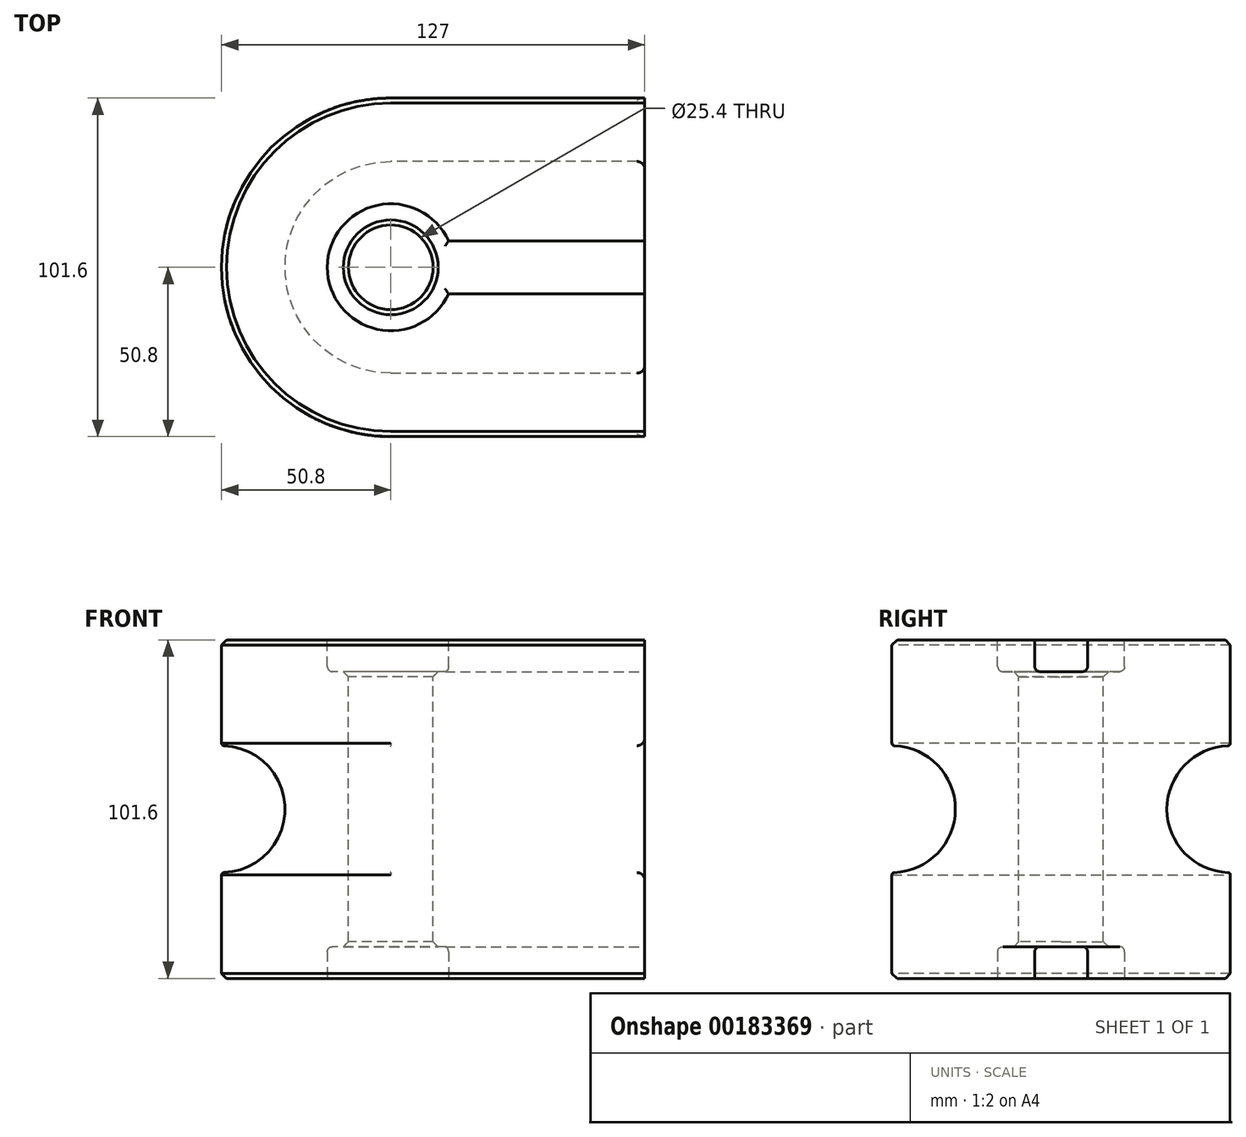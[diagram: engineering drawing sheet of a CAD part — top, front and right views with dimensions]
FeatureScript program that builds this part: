
annotation { "Feature Type Name" : "Feature", "Feature Type Description" : "" }
export const myFeature = defineFeature(function(context is Context, id is Id, definition is map)
    precondition{}
    {
        {
            var Q0;
            Q0=qCreatedBy(makeId("Top.planeOp"),FACE);
            var sketch = newSketch(context, id + "F0", { "sketchPlane" : qUnion([Q0])});
            skArc(sketch, "E0", {"start": v(0, 50.8) * mm, "mid": v(-50.8, 0) * mm, "end": v(0, -50.8) * mm});
            skLineSegment(sketch, "E1", {"start": v(0, -58.97) * mm, "end": v(0, 68.43) * mm, "construction": true});
            skLineSegment(sketch, "E2", {"start": v(0, 50.8) * mm, "end": v(76.2, 50.8) * mm});
            skLineSegment(sketch, "E3", {"start": v(76.2, 50.8) * mm, "end": v(76.2, -50.8) * mm});
            skLineSegment(sketch, "E4", {"start": v(0, -50.8) * mm, "end": v(76.2, -50.8) * mm});
            skSolve(sketch);
        }
        {
            var Q0;
            Q0 = qSketchRegion(id + "F0", true);
            extrude(context, id + "F1", {"entities" : qUnion([Q0]), "endBound" : BoundingType.SYMMETRIC, "depth" : 101.6 * mm});
        }
        {
            var Q0;
            Q0=qCreatedBy(makeId("Top.planeOp"),FACE);
            var sketch = newSketch(context, id + "F2", { "sketchPlane" : qUnion([Q0])});
            skLineSegment(sketch, "E5.0", {"start": v(-0.01, 50.8) * mm, "end": v(88.89, 50.8) * mm});
            skArc(sketch, "E6.0", {"start": v(-0.01, 50.8) * mm, "mid": v(-50.81, 0) * mm, "end": v(-0.01, -50.8) * mm});
            skLineSegment(sketch, "E7.0", {"start": v(-0.01, -50.8) * mm, "end": v(88.89, -50.8) * mm});
            skSolve(sketch);
        }
        {
            var Q0;
            Q0=sQuery(id+"F2.wireOp",VERTEX,"E5.0.end");
            var Q1;
            Q1=sQuery(id+"F2.wireOp",EDGE,"E5.0");
            cPlane(context, id + "F3", {"entities" : qUnion([Q0, Q1]), "cplaneType" : CPlaneType.LINE_POINT, "offset" : 25.4 * mm, "width" : 152.4 * mm, "height" : 152.4 * mm});
        }
        {
            var Q0;
            Q0=qCreatedBy(id+"F3.planeOp",FACE);
            var sketch = newSketch(context, id + "F4", { "sketchPlane" : qUnion([Q0])});
            skCircle(sketch, "E8", {"center": v(50.8, 0) * mm, "radius": 19.05 * mm});
            skSolve(sketch);
        }
        {
            var Q0;
            Q0=makeQuery(id+"F4.imprint","IMPRINT",FACE,{"disambiguationData":[TD([[makeQuery(id+"F4.imprint","IMPRINT",EDGE,{"derivedFrom":sQuery(id+"F4.wireOp",EDGE,"E8")}),1.0]])]});
            var Q1;
            Q1 = qConstructionFilter(qBodyType(qCreatedBy(id + "F2" ,EDGE), BodyType.WIRE), ConstructionObject.NO);
            sweep(context, id + "F5", {"operationType" : NewBodyOperationType.REMOVE, "profiles" : qUnion([Q0]), "path" : qUnion([Q1])});
        }
        {
            var Q0;
            Q0=makeQuery(id+"F1.opExtrude","CAP_FACE",FACE,{"disambiguationData":[OSD([sQuery(id+"F0.wireOp",EDGE,"E0"),sQuery(id+"F0.wireOp",EDGE,"E2"),sQuery(id+"F0.wireOp",EDGE,"E3"),sQuery(id+"F0.wireOp",EDGE,"E4")])],"isStart":false});
            var sketch = newSketch(context, id + "F6", { "sketchPlane" : qUnion([Q0])});
            skCircle(sketch, "E9", {"center": v(0, 0) * mm, "radius": 12.7 * mm});
            skSolve(sketch);
        }
        {
            var Q0;
            Q0=makeQuery(id+"F6.imprint","IMPRINT",FACE,{"disambiguationData":[TD([[makeQuery(id+"F6.imprint","IMPRINT",EDGE,{"derivedFrom":sQuery(id+"F6.wireOp",EDGE,"E9")}),1.0]])]});
            extrude(context, id + "F7", {"entities" : qUnion([Q0]), "operationType" : NewBodyOperationType.REMOVE, "endBound" : BoundingType.THROUGH_ALL, "oppositeDirection" : true, "depth" : 25.4 * mm});
        }
        {
            var Q0;
            Q0=makeQuery(id+"F1.opExtrude","CAP_FACE",FACE,{"disambiguationData":[OSD([sQuery(id+"F0.wireOp",EDGE,"E0"),sQuery(id+"F0.wireOp",EDGE,"E2"),sQuery(id+"F0.wireOp",EDGE,"E3"),sQuery(id+"F0.wireOp",EDGE,"E4")])],"isStart":false});
            var sketch = newSketch(context, id + "F8", { "sketchPlane" : qUnion([Q0])});
            skCircle(sketch, "E10", {"center": v(0, 0) * mm, "radius": 19.05 * mm});
            skSolve(sketch);
        }
        {
            var Q0;
            Q0 = qSketchRegion(id + "F8", true);
            extrude(context, id + "F9", {"entities" : qUnion([Q0]), "operationType" : NewBodyOperationType.REMOVE, "oppositeDirection" : true, "depth" : 9.52 * mm});
        }
        {
            var Q0;
            Q0=makeQuery(id+"F1.opExtrude","CAP_FACE",FACE,{"disambiguationData":[OSD([sQuery(id+"F0.wireOp",EDGE,"E0"),sQuery(id+"F0.wireOp",EDGE,"E2"),sQuery(id+"F0.wireOp",EDGE,"E3"),sQuery(id+"F0.wireOp",EDGE,"E4")])],"isStart":true});
            var sketch = newSketch(context, id + "F10", { "sketchPlane" : qUnion([Q0])});
            skCircle(sketch, "E11", {"center": v(0, 0) * mm, "radius": 19.05 * mm});
            skSolve(sketch);
        }
        {
            var Q0;
            Q0 = qSketchRegion(id + "F10", true);
            extrude(context, id + "F11", {"entities" : qUnion([Q0]), "operationType" : NewBodyOperationType.REMOVE, "oppositeDirection" : true, "depth" : 9.52 * mm});
        }
        {
            var Q0;
            Q0=makeQuery(id+"F1.opExtrude","CAP_EDGE",EDGE,{"disambiguationData":[OSD([sQuery(id+"F0.wireOp",EDGE,"E4")])],"isStart":false});
            var Q1;
            Q1=makeQuery(id+"F1.opExtrude","CAP_EDGE",EDGE,{"disambiguationData":[OSD([sQuery(id+"F0.wireOp",EDGE,"E2")])],"isStart":true});
            chamfer(context, id + "F12", {"entities" : qUnion([Q0, Q1]), "width" : 1.52 * mm, "tangentPropagation" : true});
        }
        {
            var Q0;
            Q0=makeQuery(id+"F5.boolean.opBoolean","INTERSECT",EDGE,{"disambiguationData":[OD(1.0)],"derivedFrom":[makeQuery(id+"F1.opExtrude","SWEPT_FACE",FACE,{"disambiguationData":[OSD([sQuery(id+"F0.wireOp",EDGE,"E4")])]}),makeQuery(id+"F5.opSweep","SWEPT_FACE",FACE,{"disambiguationData":[OSD([sQuery(id+"F2.wireOp",EDGE,"E7.0"),sQuery(id+"F4.wireOp",EDGE,"E8")])]})]});
            var Q1;
            Q1=makeQuery(id+"F5.boolean.opBoolean","INTERSECT",EDGE,{"disambiguationData":[OD(0.0)],"derivedFrom":[makeQuery(id+"F1.opExtrude","SWEPT_FACE",FACE,{"disambiguationData":[OSD([sQuery(id+"F0.wireOp",EDGE,"E4")])]}),makeQuery(id+"F5.opSweep","SWEPT_FACE",FACE,{"disambiguationData":[OSD([sQuery(id+"F2.wireOp",EDGE,"E7.0"),sQuery(id+"F4.wireOp",EDGE,"E8")])]})]});
            fillet(context, id + "F13", {"entities" : qUnion([Q0, Q1]), "radius" : 0.76 * mm, "tangentPropagation" : true, "allowEdgeOverflow" : false});
        }
        {
            var Q0;
            Q0=makeQuery(id+"F5.boolean.opBoolean","INTERSECT",EDGE,{"derivedFrom":[makeQuery(id+"F1.opExtrude","SWEPT_FACE",FACE,{"disambiguationData":[OSD([sQuery(id+"F0.wireOp",EDGE,"E3")])]}),makeQuery(id+"F5.opSweep","SWEPT_FACE",FACE,{"disambiguationData":[OSD([sQuery(id+"F2.wireOp",EDGE,"E5.0"),sQuery(id+"F4.wireOp",EDGE,"E8")])]})]});
            var Q1;
            Q1=makeQuery(id+"F5.boolean.opBoolean","INTERSECT",EDGE,{"derivedFrom":[makeQuery(id+"F1.opExtrude","SWEPT_FACE",FACE,{"disambiguationData":[OSD([sQuery(id+"F0.wireOp",EDGE,"E3")])]}),makeQuery(id+"F5.opSweep","SWEPT_FACE",FACE,{"disambiguationData":[OSD([sQuery(id+"F2.wireOp",EDGE,"E7.0"),sQuery(id+"F4.wireOp",EDGE,"E8")])]})]});
            fillet(context, id + "F14", {"entities" : qUnion([Q0, Q1]), "radius" : 2.3 * mm, "allowEdgeOverflow" : false});
        }
        {
            var Q0;
            Q0=makeQuery(id+"F1.opExtrude","CAP_FACE",FACE,{"disambiguationData":[OSD([sQuery(id+"F0.wireOp",EDGE,"E0"),sQuery(id+"F0.wireOp",EDGE,"E2"),sQuery(id+"F0.wireOp",EDGE,"E3"),sQuery(id+"F0.wireOp",EDGE,"E4")])],"isStart":true});
            var sketch = newSketch(context, id + "F15", { "sketchPlane" : qUnion([Q0])});
            skLineSegment(sketch, "E12.bottom", {"start": v(0, 7.94) * mm, "end": v(76.2, 7.94) * mm});
            skLineSegment(sketch, "E12.top", {"start": v(0, -7.94) * mm, "end": v(76.2, -7.94) * mm});
            skLineSegment(sketch, "E12.left", {"start": v(0, 7.94) * mm, "end": v(0, -7.94) * mm});
            skLineSegment(sketch, "E12.right", {"start": v(76.2, 7.94) * mm, "end": v(76.2, -7.94) * mm});
            skSolve(sketch);
        }
        {
            var Q0;
            Q0 = qSketchRegion(id + "F15", true);
            extrude(context, id + "F16", {"entities" : qUnion([Q0]), "operationType" : NewBodyOperationType.REMOVE, "oppositeDirection" : true, "depth" : 9.52 * mm});
        }
        {
            var Q0;
            Q0=makeQuery(id+"F1.opExtrude","CAP_FACE",FACE,{"disambiguationData":[OSD([sQuery(id+"F0.wireOp",EDGE,"E0"),sQuery(id+"F0.wireOp",EDGE,"E2"),sQuery(id+"F0.wireOp",EDGE,"E3"),sQuery(id+"F0.wireOp",EDGE,"E4")])],"isStart":false});
            var sketch = newSketch(context, id + "F17", { "sketchPlane" : qUnion([Q0])});
            skLineSegment(sketch, "E13.bottom", {"start": v(0, 7.94) * mm, "end": v(76.2, 7.94) * mm});
            skLineSegment(sketch, "E13.top", {"start": v(0, -7.94) * mm, "end": v(76.2, -7.94) * mm});
            skLineSegment(sketch, "E13.left", {"start": v(0, 7.94) * mm, "end": v(0, -7.94) * mm});
            skLineSegment(sketch, "E13.right", {"start": v(76.2, 7.94) * mm, "end": v(76.2, -7.94) * mm});
            skSolve(sketch);
        }
        {
            var Q0;
            Q0 = qSketchRegion(id + "F17", true);
            extrude(context, id + "F18", {"entities" : qUnion([Q0]), "operationType" : NewBodyOperationType.REMOVE, "oppositeDirection" : true, "depth" : 9.52 * mm});
        }
        {
            var Q0;
            Q0=makeQuery(id+"F9.boolean.opBoolean","COPY",EDGE,{"derivedFrom":makeQuery(id+"F9.opExtrude","CAP_EDGE",EDGE,{"disambiguationData":[OSD([sQuery(id+"F8.wireOp",EDGE,"E10")])],"isStart":true})});
            var Q1;
            Q1=makeQuery(id+"F18.boolean.opBoolean","COPY",EDGE,{"derivedFrom":makeQuery(id+"F18.opExtrude","CAP_EDGE",EDGE,{"disambiguationData":[OSD([sQuery(id+"F17.wireOp",EDGE,"E13.bottom")])],"isStart":true})});
            var Q2;
            Q2=makeQuery(id+"F18.boolean.opBoolean","COPY",EDGE,{"derivedFrom":makeQuery(id+"F18.opExtrude","CAP_EDGE",EDGE,{"disambiguationData":[OSD([sQuery(id+"F17.wireOp",EDGE,"E13.top")])],"isStart":true})});
            var Q3;
            Q3=makeQuery(id+"F9.boolean.opBoolean","INTERSECT",EDGE,{"derivedFrom":[makeQuery(id+"F7.boolean.opBoolean","COPY",FACE,{"derivedFrom":makeQuery(id+"F7.opExtrude","SWEPT_FACE",FACE,{"disambiguationData":[OSD([sQuery(id+"F6.wireOp",EDGE,"E9")])]})}),makeQuery(id+"F9.opExtrude","CAP_FACE",FACE,{"disambiguationData":[OSD([sQuery(id+"F8.wireOp",EDGE,"E10")])],"isStart":false})]});
            var Q4;
            Q4=makeQuery(id+"F11.boolean.opBoolean","COPY",EDGE,{"derivedFrom":makeQuery(id+"F11.opExtrude","CAP_EDGE",EDGE,{"disambiguationData":[OSD([sQuery(id+"F10.wireOp",EDGE,"E11")])],"isStart":true})});
            var Q5;
            Q5=makeQuery(id+"F11.boolean.opBoolean","INTERSECT",EDGE,{"derivedFrom":[makeQuery(id+"F7.boolean.opBoolean","COPY",FACE,{"derivedFrom":makeQuery(id+"F7.opExtrude","SWEPT_FACE",FACE,{"disambiguationData":[OSD([sQuery(id+"F6.wireOp",EDGE,"E9")])]})}),makeQuery(id+"F11.opExtrude","CAP_FACE",FACE,{"disambiguationData":[OSD([sQuery(id+"F10.wireOp",EDGE,"E11")])],"isStart":false})]});
            var Q6;
            Q6=makeQuery(id+"F16.boolean.opBoolean","COPY",EDGE,{"derivedFrom":makeQuery(id+"F16.opExtrude","CAP_EDGE",EDGE,{"disambiguationData":[OSD([sQuery(id+"F15.wireOp",EDGE,"E12.bottom")])],"isStart":true})});
            var Q7;
            Q7=makeQuery(id+"F16.boolean.opBoolean","COPY",EDGE,{"derivedFrom":makeQuery(id+"F16.opExtrude","CAP_EDGE",EDGE,{"disambiguationData":[OSD([sQuery(id+"F15.wireOp",EDGE,"E12.top")])],"isStart":true})});
            chamfer(context, id + "F19", {"entities" : qUnion([Q0, Q1, Q2, Q3, Q4, Q5, Q6, Q7]), "width" : 1.52 * mm, "tangentPropagation" : true});
        }
        {
            var Q0;
            Q0=makeQuery(id+"F11.boolean.opBoolean","COPY",EDGE,{"derivedFrom":makeQuery(id+"F11.opExtrude","CAP_EDGE",EDGE,{"disambiguationData":[OSD([sQuery(id+"F10.wireOp",EDGE,"E11")])],"isStart":false})});
            var Q1;
            Q1=makeQuery(id+"F16.boolean.opBoolean","COPY",EDGE,{"derivedFrom":makeQuery(id+"F16.opExtrude","CAP_EDGE",EDGE,{"disambiguationData":[OSD([sQuery(id+"F15.wireOp",EDGE,"E12.bottom")])],"isStart":false})});
            var Q2;
            Q2=makeQuery(id+"F16.boolean.opBoolean","COPY",EDGE,{"derivedFrom":makeQuery(id+"F16.opExtrude","CAP_EDGE",EDGE,{"disambiguationData":[OSD([sQuery(id+"F15.wireOp",EDGE,"E12.top")])],"isStart":false})});
            var Q3;
            Q3=makeQuery(id+"F9.boolean.opBoolean","COPY",EDGE,{"derivedFrom":makeQuery(id+"F9.opExtrude","CAP_EDGE",EDGE,{"disambiguationData":[OSD([sQuery(id+"F8.wireOp",EDGE,"E10")])],"isStart":false})});
            var Q4;
            Q4=makeQuery(id+"F18.boolean.opBoolean","COPY",EDGE,{"derivedFrom":makeQuery(id+"F18.opExtrude","CAP_EDGE",EDGE,{"disambiguationData":[OSD([sQuery(id+"F17.wireOp",EDGE,"E13.bottom")])],"isStart":false})});
            var Q5;
            Q5=makeQuery(id+"F18.boolean.opBoolean","COPY",EDGE,{"derivedFrom":makeQuery(id+"F18.opExtrude","CAP_EDGE",EDGE,{"disambiguationData":[OSD([sQuery(id+"F17.wireOp",EDGE,"E13.top")])],"isStart":false})});
            fillet(context, id + "F20", {"entities" : qUnion([Q0, Q1, Q2, Q3, Q4, Q5]), "radius" : 1.52 * mm, "tangentPropagation" : true, "allowEdgeOverflow" : false});
        }
    });
